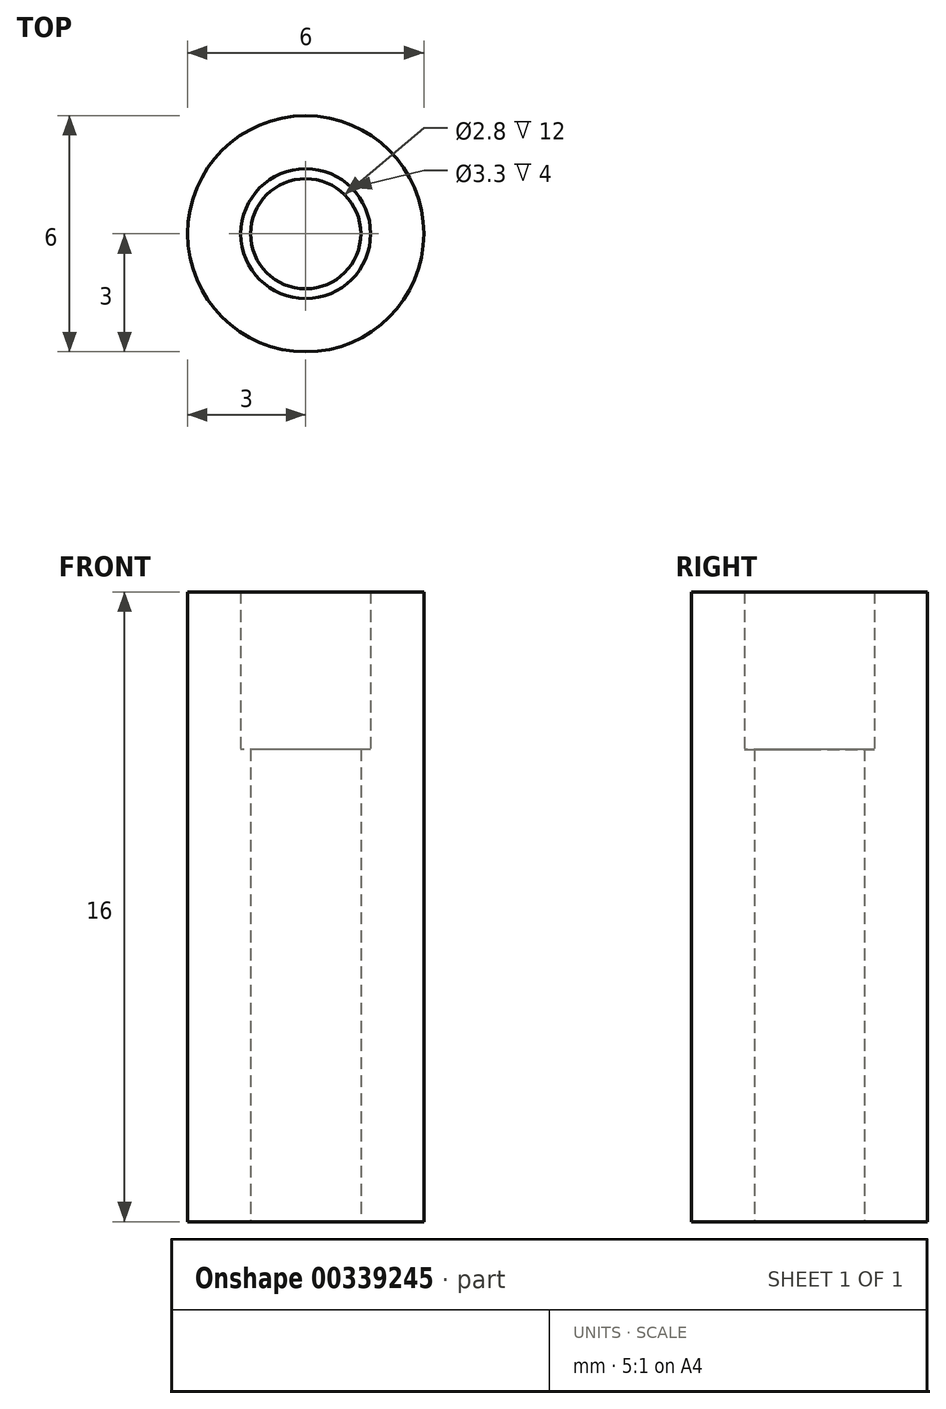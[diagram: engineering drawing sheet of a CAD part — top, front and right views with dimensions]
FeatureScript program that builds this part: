
annotation { "Feature Type Name" : "Feature", "Feature Type Description" : "" }
export const myFeature = defineFeature(function(context is Context, id is Id, definition is map)
    precondition{}
    {
        {
            var Q0;
            Q0=qCreatedBy(makeId("Top.planeOp"),FACE);
            var sketch = newSketch(context, id + "F0", { "sketchPlane" : qUnion([Q0])});
            skCircle(sketch, "E0", {"center": v(0, 0) * mm, "radius": 1.4 * mm});
            skCircle(sketch, "E1", {"center": v(0, 0) * mm, "radius": 3 * mm});
            skSolve(sketch);
        }
        {
            var Q0;
            Q0=makeQuery(id+"F0.imprint","IMPRINT",FACE,{"disambiguationData":[TD([[makeQuery(id+"F0.imprint","IMPRINT",EDGE,{"derivedFrom":sQuery(id+"F0.wireOp",EDGE,"E0")}),-1.0]])]});
            extrude(context, id + "F1", {"entities" : qUnion([Q0]), "depth" : 12 * mm});
        }
        {
            var Q0;
            Q0=makeQuery(id+"F1.opExtrude","CAP_FACE",FACE,{"disambiguationData":[OSD([sQuery(id+"F0.wireOp",EDGE,"E0"),sQuery(id+"F0.wireOp",EDGE,"E1")])],"isStart":false});
            var sketch = newSketch(context, id + "F2", { "sketchPlane" : qUnion([Q0])});
            skCircle(sketch, "E2.0.0", {"center": v(0, 0) * mm, "radius": 3 * mm});
            skCircle(sketch, "E3", {"center": v(0, 0) * mm, "radius": 1.65 * mm});
            skSolve(sketch);
        }
        {
            var Q0;
            Q0=makeQuery(id+"F2.imprint","IMPRINT",FACE,{"disambiguationData":[TD([[makeQuery(id+"F2.imprint","IMPRINT",EDGE,{"derivedFrom":sQuery(id+"F2.wireOp",EDGE,"E2.0.0")}),1.0]])]});
            extrude(context, id + "F3", {"entities" : qUnion([Q0]), "operationType" : NewBodyOperationType.ADD, "depth" : 4 * mm});
        }
    });
